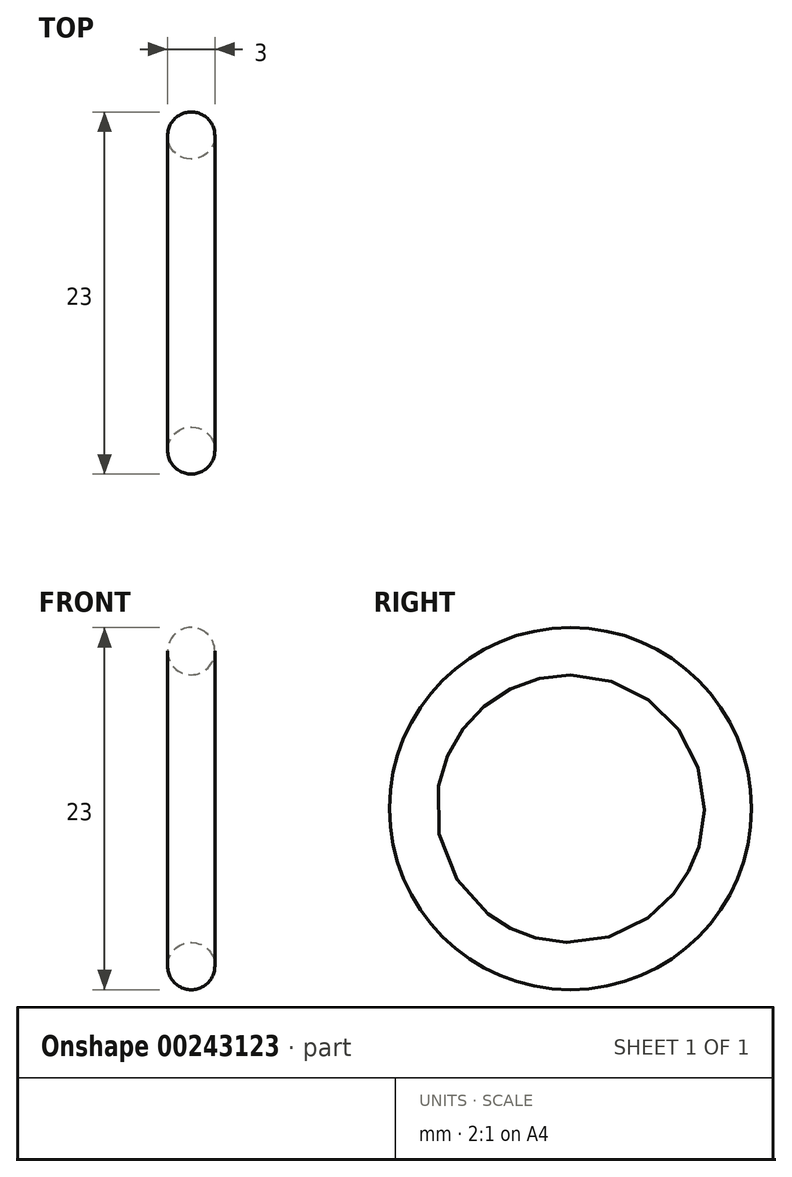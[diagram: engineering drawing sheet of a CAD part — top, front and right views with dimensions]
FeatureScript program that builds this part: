
annotation { "Feature Type Name" : "Feature", "Feature Type Description" : "" }
export const myFeature = defineFeature(function(context is Context, id is Id, definition is map)
    precondition{}
    {
        {
            var Q0;
            Q0=qCreatedBy(makeId("Top.planeOp"),FACE);
            var sketch = newSketch(context, id + "F0", { "sketchPlane" : qUnion([Q0])});
            skLineSegment(sketch, "E0", {"start": v(0, 0) * mm, "end": v(10, 0) * mm});
            skLineSegment(sketch, "E1", {"start": v(0, 0) * mm, "end": v(0, 10) * mm});
            skCircle(sketch, "E2", {"center": v(10, 0) * mm, "radius": 1.5 * mm});
            skCircle(sketch, "E3", {"center": v(0, 10) * mm, "radius": 1.5 * mm});
            skSolve(sketch);
        }
        {
            var Q0;
            Q0=makeQuery(id+"F0.imprint","IMPRINT",FACE,{"disambiguationData":[TD([[makeQuery(id+"F0.imprint","IMPRINT",EDGE,{"derivedFrom":sQuery(id+"F0.wireOp",EDGE,"E3")}),1.0]])]});
            var Q1;
            Q1=sQuery(id+"F0.wireOp",EDGE,"E0");
            revolve(context, id + "F1", {"entities" : qUnion([Q0]), "axis" : qUnion([Q1]), "revolveType" : RevolveType.FULL});
        }
    });
